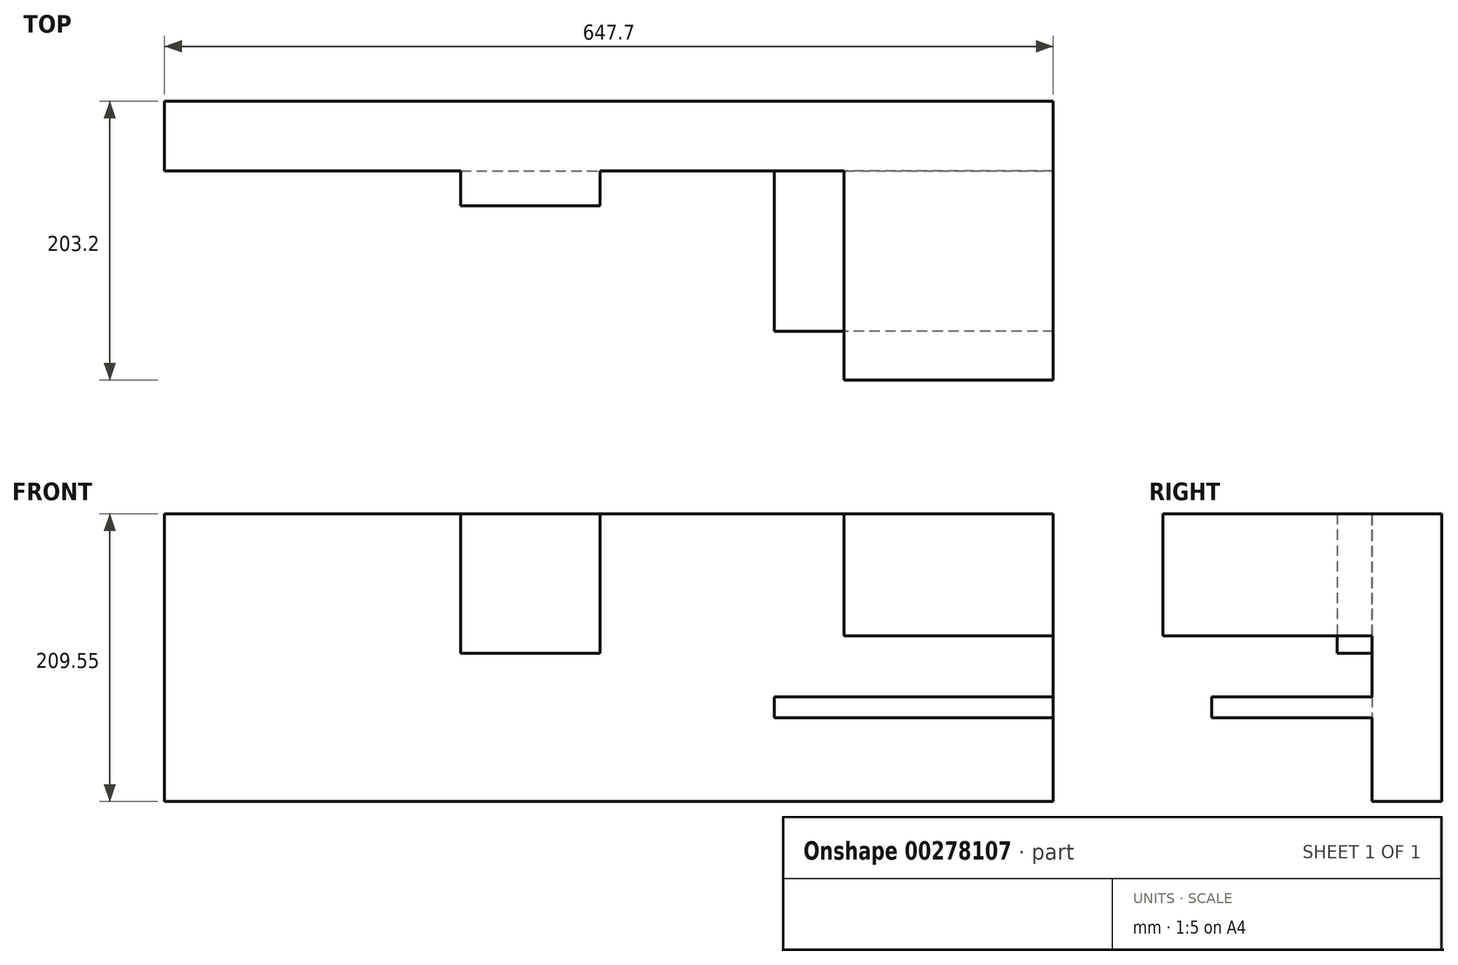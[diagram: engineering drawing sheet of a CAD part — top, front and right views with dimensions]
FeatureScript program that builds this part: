
annotation { "Feature Type Name" : "Feature", "Feature Type Description" : "" }
export const myFeature = defineFeature(function(context is Context, id is Id, definition is map)
    precondition{}
    {
        {
            var Q0;
            Q0=qCreatedBy(makeId("Front.planeOp"),FACE);
            var sketch = newSketch(context, id + "F0", { "sketchPlane" : qUnion([Q0])});
            skLineSegment(sketch, "E0.bottom", {"start": v(0, 0) * mm, "end": v(647.7, 0) * mm});
            skLineSegment(sketch, "E0.top", {"start": v(0, 209.55) * mm, "end": v(647.7, 209.55) * mm});
            skLineSegment(sketch, "E0.left", {"start": v(0, 0) * mm, "end": v(0, 209.55) * mm});
            skLineSegment(sketch, "E0.right", {"start": v(647.7, 0) * mm, "end": v(647.7, 209.55) * mm});
            skSolve(sketch);
        }
        {
            var Q0;
            Q0 = qSketchRegion(id + "F0", true);
            extrude(context, id + "F1", {"entities" : qUnion([Q0]), "depth" : 50.8 * mm});
        }
        {
            var Q0;
            Q0=makeQuery(id+"F1.opExtrude","CAP_FACE",FACE,{"disambiguationData":[OSD([sQuery(id+"F0.wireOp",EDGE,"E0.bottom"),sQuery(id+"F0.wireOp",EDGE,"E0.top"),sQuery(id+"F0.wireOp",EDGE,"E0.left"),sQuery(id+"F0.wireOp",EDGE,"E0.right")])],"isStart":false});
            var sketch = newSketch(context, id + "F2", { "sketchPlane" : qUnion([Q0])});
            skLineSegment(sketch, "E1.bottom", {"start": v(215.9, 209.55) * mm, "end": v(317.5, 209.55) * mm});
            skLineSegment(sketch, "E1.top", {"start": v(215.9, 107.95) * mm, "end": v(317.5, 107.95) * mm});
            skLineSegment(sketch, "E1.left", {"start": v(215.9, 209.55) * mm, "end": v(215.9, 107.95) * mm});
            skLineSegment(sketch, "E1.right", {"start": v(317.5, 209.55) * mm, "end": v(317.5, 107.95) * mm});
            skSolve(sketch);
        }
        {
            var Q0;
            Q0=makeQuery(id+"F2.imprint","IMPRINT",FACE,{"disambiguationData":[TD([[makeQuery(id+"F2.imprint","IMPRINT",EDGE,{"derivedFrom":sQuery(id+"F2.wireOp",EDGE,"E1.bottom")}),-1.0]])]});
            extrude(context, id + "F3", {"entities" : qUnion([Q0]), "operationType" : NewBodyOperationType.ADD, "depth" : 25.4 * mm});
        }
        {
            var Q0;
            Q0=makeQuery(id+"F1.opExtrude","CAP_FACE",FACE,{"disambiguationData":[OSD([sQuery(id+"F0.wireOp",EDGE,"E0.bottom"),sQuery(id+"F0.wireOp",EDGE,"E0.top"),sQuery(id+"F0.wireOp",EDGE,"E0.left"),sQuery(id+"F0.wireOp",EDGE,"E0.right")])],"isStart":false});
            var sketch = newSketch(context, id + "F4", { "sketchPlane" : qUnion([Q0])});
            skLineSegment(sketch, "E2.bottom", {"start": v(647.7, 76.2) * mm, "end": v(444.5, 76.2) * mm});
            skLineSegment(sketch, "E2.top", {"start": v(647.7, 60.96) * mm, "end": v(444.5, 60.96) * mm});
            skLineSegment(sketch, "E2.left", {"start": v(647.7, 76.2) * mm, "end": v(647.7, 60.96) * mm});
            skLineSegment(sketch, "E2.right", {"start": v(444.5, 76.2) * mm, "end": v(444.5, 60.96) * mm});
            skSolve(sketch);
        }
        {
            var Q0;
            Q0 = qSketchRegion(id + "F4", true);
            extrude(context, id + "F5", {"entities" : qUnion([Q0]), "operationType" : NewBodyOperationType.ADD, "depth" : 116.84 * mm});
        }
        {
            var Q0;
            Q0=makeQuery(id+"F1.opExtrude","CAP_FACE",FACE,{"disambiguationData":[OSD([sQuery(id+"F0.wireOp",EDGE,"E0.bottom"),sQuery(id+"F0.wireOp",EDGE,"E0.top"),sQuery(id+"F0.wireOp",EDGE,"E0.left"),sQuery(id+"F0.wireOp",EDGE,"E0.right")])],"isStart":false});
            var sketch = newSketch(context, id + "F6", { "sketchPlane" : qUnion([Q0])});
            skLineSegment(sketch, "E3.bottom", {"start": v(495.3, 120.65) * mm, "end": v(647.7, 120.65) * mm});
            skLineSegment(sketch, "E3.top", {"start": v(495.3, 209.55) * mm, "end": v(647.7, 209.55) * mm});
            skLineSegment(sketch, "E3.left", {"start": v(495.3, 120.65) * mm, "end": v(495.3, 209.55) * mm});
            skLineSegment(sketch, "E3.right", {"start": v(647.7, 120.65) * mm, "end": v(647.7, 209.55) * mm});
            skSolve(sketch);
        }
        {
            var Q0;
            Q0 = qSketchRegion(id + "F6", true);
            extrude(context, id + "F7", {"entities" : qUnion([Q0]), "operationType" : NewBodyOperationType.ADD, "depth" : 152.4 * mm});
        }
    });
